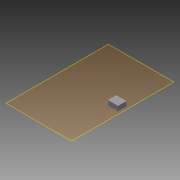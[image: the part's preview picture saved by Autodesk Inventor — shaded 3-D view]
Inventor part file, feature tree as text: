
AUTODESK INVENTOR PART (.ipt)
format: ipt  version: 2013 SP2 (Build 170200200, 200)  size: 101,376 bytes
history: native  units: mm
features: extrude x3, sketch x3, plane x1
ambient origin geometry x8: Origin, YZ Plane, XZ Plane, XY Plane, X Axis, Y Axis, Z Axis, Center Point
bodies: Solid1 (feature_tree)
feature tree (7):
  plane  "Work Plane1"
  extrude  "Extrusion1"  Depth=9.0mm
  extrude  "Extrusion2"  Depth=6.2mm
  extrude  "Extrusion3"  Depth=3.5mm
  sketch  "Sketch1"  dims[d0=11.0mm d2=9.0mm]
  sketch  "Sketch2"  dims[d3=5.0mm d4=0.0mm d5=6.2mm]
  sketch  "Sketch3"  dims[d7=4.0mm d8=0.0mm d9=3.5mm d11=7.0mm d12=0.0mm]
